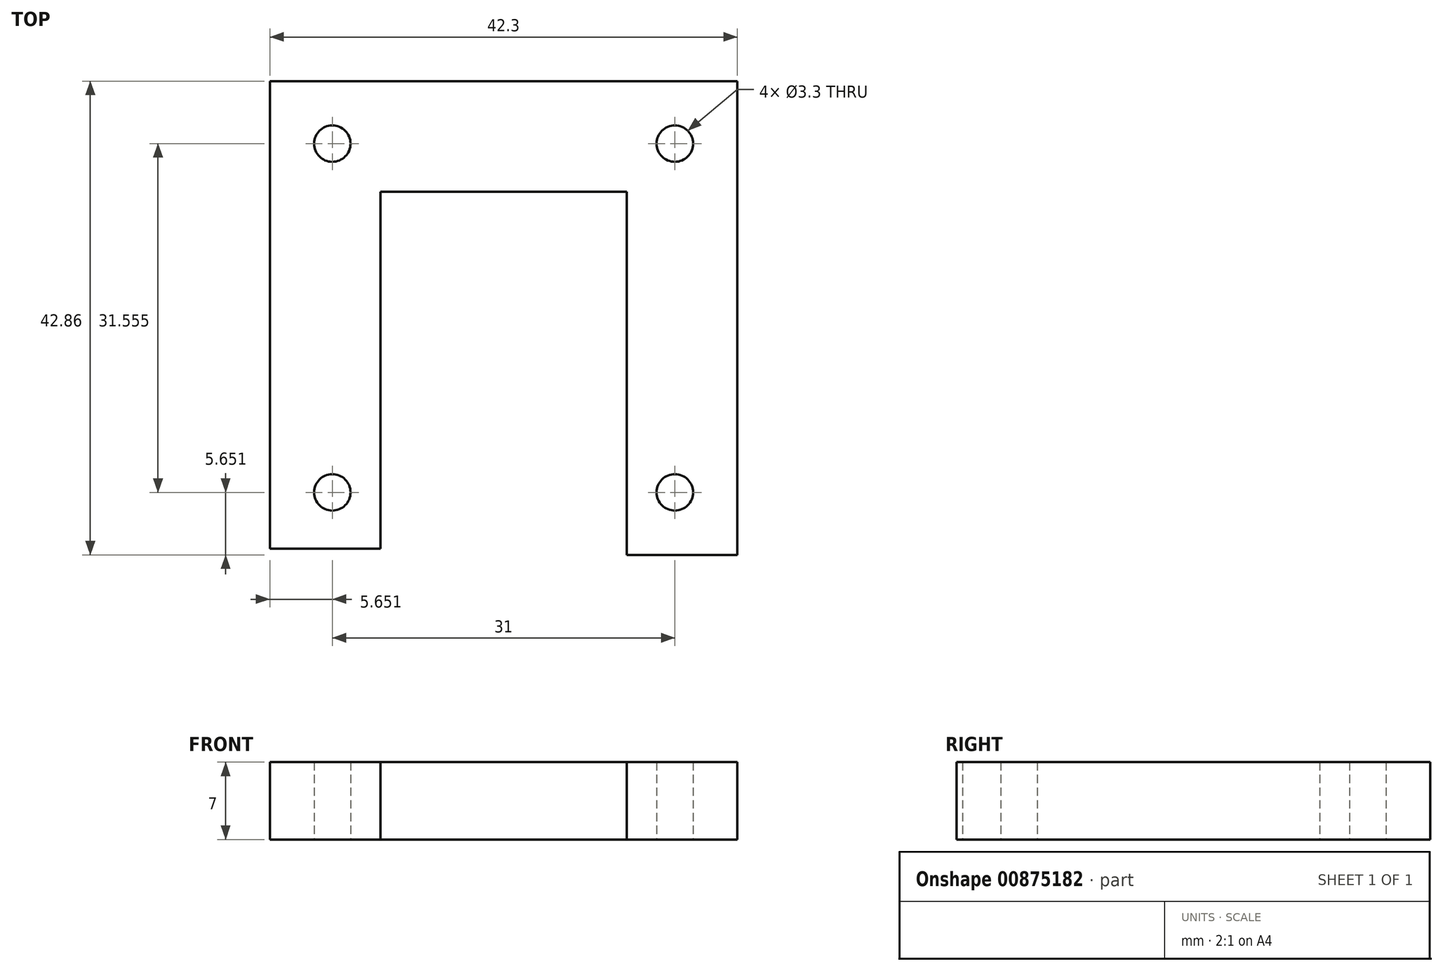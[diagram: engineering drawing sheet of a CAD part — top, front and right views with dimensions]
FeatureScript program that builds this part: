
annotation { "Feature Type Name" : "Feature", "Feature Type Description" : "" }
export const myFeature = defineFeature(function(context is Context, id is Id, definition is map)
    precondition{}
    {
        {
            var Q0;
            Q0=qCreatedBy(makeId("Top.planeOp"),FACE);
            var sketch = newSketch(context, id + "F0", { "sketchPlane" : qUnion([Q0])});
            skLineSegment(sketch, "E0.bottom", {"start": v(-20.44, 22.36) * mm, "end": v(21.86, 22.36) * mm});
            skLineSegment(sketch, "E0.left", {"start": v(-20.44, 22.36) * mm, "end": v(-20.44, -19.94) * mm});
            skLineSegment(sketch, "E0.right", {"start": v(21.86, 22.36) * mm, "end": v(21.86, -20.5) * mm});
            skPoint(sketch, "E1", {"position": v(-14.79, 16.7) * mm});
            skPoint(sketch, "E2", {"position": v(16.21, 16.7) * mm});
            skPoint(sketch, "E3", {"position": v(16.21, -14.85) * mm});
            skPoint(sketch, "E4", {"position": v(-14.79, -14.85) * mm});
            skLineSegment(sketch, "E5.0", {"start": v(-10.44, 22.36) * mm, "end": v(-10.44, -19.94) * mm});
            skLineSegment(sketch, "E6.0", {"start": v(11.86, 22.36) * mm, "end": v(11.86, -20.5) * mm});
            skLineSegment(sketch, "E7", {"start": v(-20.44, -19.94) * mm, "end": v(-10.44, -19.94) * mm});
            skLineSegment(sketch, "E8", {"start": v(11.86, -20.5) * mm, "end": v(21.86, -20.5) * mm});
            skLineSegment(sketch, "E9.0", {"start": v(-20.44, 12.36) * mm, "end": v(21.86, 12.36) * mm});
            skSolve(sketch);
        }
        {
            var Q0;
            Q0 = qSketchRegion(id + "F0", true);
            extrude(context, id + "F1", {"entities" : qUnion([Q0]), "depth" : 7 * mm, "offsetDistance" : 25 * mm});
        }
        {
            var Q0;
            Q0=sQuery(id+"F0.wireOp",VERTEX,"E1");
            var Q1;
            Q1=sQuery(id+"F0.wireOp",VERTEX,"E2");
            var Q2;
            Q2=sQuery(id+"F0.wireOp",VERTEX,"E4");
            var Q3;
            Q3=sQuery(id+"F0.wireOp",VERTEX,"E3");
            var Q4;
            Q4=makeQuery(id+"F1.opExtrude","SWEPT_BODY",BODY,{"disambiguationData":[OSD([sQuery(id+"F0.wireOp",EDGE,"E0.bottom"),sQuery(id+"F0.wireOp",EDGE,"E0.left"),sQuery(id+"F0.wireOp",EDGE,"E0.right"),sQuery(id+"F0.wireOp",EDGE,"317e0009-5c04-481a-b118-b73622342ea3.0"),sQuery(id+"F0.wireOp",EDGE,"E5.0"),sQuery(id+"F0.wireOp",EDGE,"E6.0"),sQuery(id+"F0.wireOp",EDGE,"E7"),sQuery(id+"F0.wireOp",EDGE,"E8")])]});
            hole(context, id + "F2", {"style" : HoleStyle.SIMPLE, "endStyle" : HoleEndStyle.THROUGH, "oppositeDirection" : true, "holeDiameter" : 3.3 * mm, "majorDiameter" : 5 * mm, "isTappedThrough" : true, "tappedDepth" : 12 * mm, "tapClearance" : 3, "locations" : qUnion([Q0, Q1, Q2, Q3]), "scope" : qUnion([Q4])});
        }
    });
